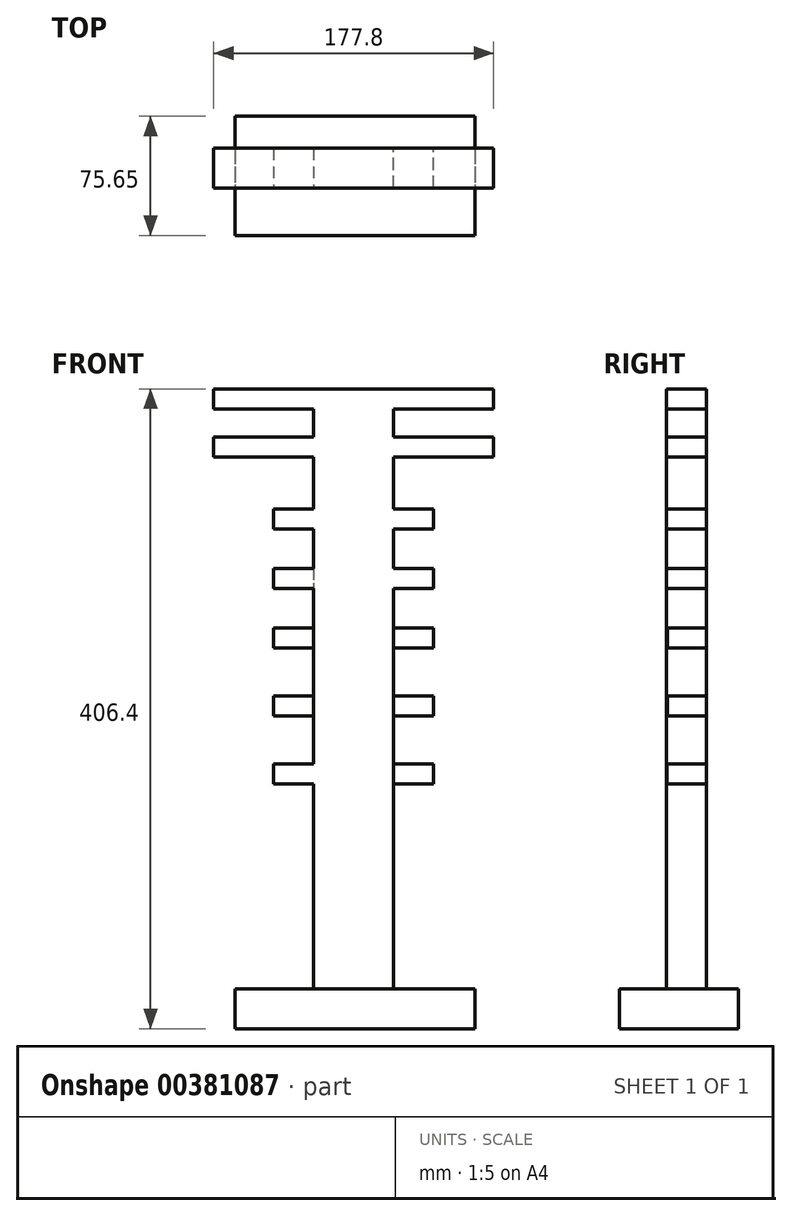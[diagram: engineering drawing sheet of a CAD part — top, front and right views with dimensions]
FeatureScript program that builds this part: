
annotation { "Feature Type Name" : "Feature", "Feature Type Description" : "" }
export const myFeature = defineFeature(function(context is Context, id is Id, definition is map)
    precondition{}
    {
        {
            var Q0;
            Q0=qCreatedBy(makeId("Top.planeOp"),FACE);
            var sketch = newSketch(context, id + "F0", { "sketchPlane" : qUnion([Q0])});
            skLineSegment(sketch, "E0.bottom", {"start": v(-76.2, 0) * mm, "end": v(76.2, 0) * mm});
            skLineSegment(sketch, "E0.top", {"start": v(-76.2, -75.65) * mm, "end": v(76.2, -75.65) * mm});
            skLineSegment(sketch, "E0.left", {"start": v(-76.2, 0) * mm, "end": v(-76.2, -75.65) * mm});
            skLineSegment(sketch, "E0.right", {"start": v(76.2, 0) * mm, "end": v(76.2, -75.65) * mm});
            skSolve(sketch);
        }
        {
            var Q0;
            Q0=makeQuery(id+"F0.imprint","IMPRINT",FACE,{"disambiguationData":[TD([[makeQuery(id+"F0.imprint","IMPRINT",EDGE,{"derivedFrom":sQuery(id+"F0.wireOp",EDGE,"E0.bottom")}),-1.0]])]});
            extrude(context, id + "F1", {"entities" : qUnion([Q0]), "depth" : 25.4 * mm});
        }
        {
            var Q0;
            Q0=makeQuery(id+"F1.opExtrude","CAP_FACE",FACE,{"disambiguationData":[OSD([sQuery(id+"F0.wireOp",EDGE,"E0.bottom"),sQuery(id+"F0.wireOp",EDGE,"E0.top"),sQuery(id+"F0.wireOp",EDGE,"E0.left"),sQuery(id+"F0.wireOp",EDGE,"E0.right")])],"isStart":false});
            var sketch = newSketch(context, id + "F2", { "sketchPlane" : qUnion([Q0])});
            skLineSegment(sketch, "E1.bottom", {"start": v(-26.33, -20.36) * mm, "end": v(24.47, -20.36) * mm});
            skLineSegment(sketch, "E1.top", {"start": v(-26.33, -45.76) * mm, "end": v(24.47, -45.76) * mm});
            skLineSegment(sketch, "E1.left", {"start": v(-26.33, -20.36) * mm, "end": v(-26.33, -45.76) * mm});
            skLineSegment(sketch, "E1.right", {"start": v(24.47, -20.36) * mm, "end": v(24.47, -45.76) * mm});
            skSolve(sketch);
        }
        {
            var Q0;
            Q0=makeQuery(id+"F2.imprint","IMPRINT",FACE,{"disambiguationData":[TD([[makeQuery(id+"F2.imprint","IMPRINT",EDGE,{"derivedFrom":sQuery(id+"F2.wireOp",EDGE,"E1.bottom")}),-1.0]])]});
            extrude(context, id + "F3", {"entities" : qUnion([Q0]), "operationType" : NewBodyOperationType.ADD, "depth" : 381 * mm});
        }
        {
            var Q0;
            Q0=makeQuery(id+"F3.opExtrude","SWEPT_FACE",FACE,{"disambiguationData":[OSD([sQuery(id+"F2.wireOp",EDGE,"E1.right")])]});
            var sketch = newSketch(context, id + "F4", { "sketchPlane" : qUnion([Q0])});
            skLineSegment(sketch, "E2.bottom", {"start": v(-45.76, 406.4) * mm, "end": v(-20.36, 406.4) * mm});
            skLineSegment(sketch, "E2.top", {"start": v(-45.76, 393.7) * mm, "end": v(-20.36, 393.7) * mm});
            skLineSegment(sketch, "E2.left", {"start": v(-45.76, 406.4) * mm, "end": v(-45.76, 393.7) * mm});
            skLineSegment(sketch, "E2.right", {"start": v(-20.36, 406.4) * mm, "end": v(-20.36, 393.7) * mm});
            skSolve(sketch);
        }
        {
            var Q0;
            Q0=makeQuery(id+"F4.imprint","IMPRINT",FACE,{"disambiguationData":[TD([[makeQuery(id+"F4.imprint","IMPRINT",EDGE,{"derivedFrom":sQuery(id+"F4.wireOp",EDGE,"E2.bottom")}),1.0]])]});
            extrude(context, id + "F5", {"entities" : qUnion([Q0]), "operationType" : NewBodyOperationType.ADD, "depth" : 63.5 * mm});
        }
        {
            var Q0;
            Q0=makeQuery(id+"F3.opExtrude","SWEPT_FACE",FACE,{"disambiguationData":[OSD([sQuery(id+"F2.wireOp",EDGE,"E1.right")])]});
            var sketch = newSketch(context, id + "F6", { "sketchPlane" : qUnion([Q0])});
            skLineSegment(sketch, "E3.bottom", {"start": v(-45.76, 375.92) * mm, "end": v(-20.36, 375.92) * mm});
            skLineSegment(sketch, "E3.top", {"start": v(-45.76, 363.22) * mm, "end": v(-20.36, 363.22) * mm});
            skLineSegment(sketch, "E3.left", {"start": v(-45.76, 375.92) * mm, "end": v(-45.76, 363.22) * mm});
            skLineSegment(sketch, "E3.right", {"start": v(-20.36, 375.92) * mm, "end": v(-20.36, 363.22) * mm});
            skSolve(sketch);
        }
        {
            var Q0;
            Q0=makeQuery(id+"F6.imprint","IMPRINT",FACE,{"disambiguationData":[TD([[makeQuery(id+"F6.imprint","IMPRINT",EDGE,{"derivedFrom":sQuery(id+"F6.wireOp",EDGE,"E3.bottom")}),-1.0]])]});
            extrude(context, id + "F7", {"entities" : qUnion([Q0]), "operationType" : NewBodyOperationType.ADD, "depth" : 63.5 * mm});
        }
        {
            var Q0;
            Q0=makeQuery(id+"F3.opExtrude","SWEPT_FACE",FACE,{"disambiguationData":[OSD([sQuery(id+"F2.wireOp",EDGE,"E1.left")])]});
            var sketch = newSketch(context, id + "F8", { "sketchPlane" : qUnion([Q0])});
            skLineSegment(sketch, "E4.bottom", {"start": v(20.36, 406.4) * mm, "end": v(45.76, 406.4) * mm});
            skLineSegment(sketch, "E4.top", {"start": v(20.36, 393.7) * mm, "end": v(45.76, 393.7) * mm});
            skLineSegment(sketch, "E4.left", {"start": v(20.36, 406.4) * mm, "end": v(20.36, 393.7) * mm});
            skLineSegment(sketch, "E4.right", {"start": v(45.76, 406.4) * mm, "end": v(45.76, 393.7) * mm});
            skSolve(sketch);
        }
        {
            var Q0;
            Q0=makeQuery(id+"F8.imprint","IMPRINT",FACE,{"disambiguationData":[TD([[makeQuery(id+"F8.imprint","IMPRINT",EDGE,{"derivedFrom":sQuery(id+"F8.wireOp",EDGE,"E4.bottom")}),-1.0]])]});
            extrude(context, id + "F9", {"entities" : qUnion([Q0]), "operationType" : NewBodyOperationType.ADD, "depth" : 63.5 * mm});
        }
        {
            var Q0;
            Q0=makeQuery(id+"F3.opExtrude","SWEPT_FACE",FACE,{"disambiguationData":[OSD([sQuery(id+"F2.wireOp",EDGE,"E1.left")])]});
            var sketch = newSketch(context, id + "F10", { "sketchPlane" : qUnion([Q0])});
            skLineSegment(sketch, "E5.bottom", {"start": v(20.36, 375.92) * mm, "end": v(45.76, 375.92) * mm});
            skLineSegment(sketch, "E5.top", {"start": v(20.36, 363.22) * mm, "end": v(45.76, 363.22) * mm});
            skLineSegment(sketch, "E5.left", {"start": v(20.36, 375.92) * mm, "end": v(20.36, 363.22) * mm});
            skLineSegment(sketch, "E5.right", {"start": v(45.76, 375.92) * mm, "end": v(45.76, 363.22) * mm});
            skSolve(sketch);
        }
        {
            var Q0;
            Q0=makeQuery(id+"F10.imprint","IMPRINT",FACE,{"disambiguationData":[TD([[makeQuery(id+"F10.imprint","IMPRINT",EDGE,{"derivedFrom":sQuery(id+"F10.wireOp",EDGE,"E5.bottom")}),-1.0]])]});
            extrude(context, id + "F11", {"entities" : qUnion([Q0]), "operationType" : NewBodyOperationType.ADD, "depth" : 63.5 * mm});
        }
        {
            var Q0;
            Q0=makeQuery(id+"F7.boolean.opBoolean","SPLIT",FACE,{"disambiguationData":[TD([makeQuery(id+"F7.opExtrude","SWEPT_FACE",FACE,{"disambiguationData":[OSD([sQuery(id+"F6.wireOp",EDGE,"E3.top")])]})])],"derivedFrom":makeQuery(id+"F3.opExtrude","SWEPT_FACE",FACE,{"disambiguationData":[OSD([sQuery(id+"F2.wireOp",EDGE,"E1.right")])]})});
            var sketch = newSketch(context, id + "F12", { "sketchPlane" : qUnion([Q0])});
            skLineSegment(sketch, "E6.bottom", {"start": v(-45.76, 330.2) * mm, "end": v(-20.36, 330.2) * mm});
            skLineSegment(sketch, "E6.top", {"start": v(-45.76, 317.5) * mm, "end": v(-20.36, 317.5) * mm});
            skLineSegment(sketch, "E6.left", {"start": v(-45.76, 330.2) * mm, "end": v(-45.76, 317.5) * mm});
            skLineSegment(sketch, "E6.right", {"start": v(-20.36, 330.2) * mm, "end": v(-20.36, 317.5) * mm});
            skSolve(sketch);
        }
        {
            var Q0;
            Q0=makeQuery(id+"F12.imprint","IMPRINT",FACE,{"disambiguationData":[TD([[makeQuery(id+"F12.imprint","IMPRINT",EDGE,{"derivedFrom":sQuery(id+"F12.wireOp",EDGE,"E6.bottom")}),-1.0]])]});
            extrude(context, id + "F13", {"entities" : qUnion([Q0]), "operationType" : NewBodyOperationType.ADD, "depth" : 25.4 * mm});
        }
        {
            var Q0;
            Q0=makeQuery(id+"F13.boolean.opBoolean","SPLIT",FACE,{"disambiguationData":[TD([makeQuery(id+"F13.opExtrude","SWEPT_FACE",FACE,{"disambiguationData":[OSD([sQuery(id+"F12.wireOp",EDGE,"E6.top")])]})])],"derivedFrom":makeQuery(id+"F7.boolean.opBoolean","SPLIT",FACE,{"disambiguationData":[TD([makeQuery(id+"F7.opExtrude","SWEPT_FACE",FACE,{"disambiguationData":[OSD([sQuery(id+"F6.wireOp",EDGE,"E3.top")])]})])],"derivedFrom":makeQuery(id+"F3.opExtrude","SWEPT_FACE",FACE,{"disambiguationData":[OSD([sQuery(id+"F2.wireOp",EDGE,"E1.right")])]})})});
            var sketch = newSketch(context, id + "F14", { "sketchPlane" : qUnion([Q0])});
            skLineSegment(sketch, "E7.bottom", {"start": v(-45.76, 292.35) * mm, "end": v(-20.36, 292.35) * mm});
            skLineSegment(sketch, "E7.top", {"start": v(-45.76, 279.65) * mm, "end": v(-20.36, 279.65) * mm});
            skLineSegment(sketch, "E7.left", {"start": v(-45.76, 292.35) * mm, "end": v(-45.76, 279.65) * mm});
            skLineSegment(sketch, "E7.right", {"start": v(-20.36, 292.35) * mm, "end": v(-20.36, 279.65) * mm});
            skSolve(sketch);
        }
        {
            var Q0;
            {var subQ0=sQuery(id+"F14.wireOp",EDGE,"E7.top");Q0=makeQuery(id+"F14.imprint","IMPRINT",FACE,{"disambiguationData":[TD([[makeQuery(id+"F14.imprint","IMPRINT",EDGE,{"derivedFrom":subQ0}),-1.0]])]});}
            var sketch = newSketch(context, id + "F15", { "sketchPlane" : qUnion([Q0])});
            skLineSegment(sketch, "E8.bottom", {"start": v(-45.28, 254.5) * mm, "end": v(-19.88, 254.5) * mm});
            skLineSegment(sketch, "E8.top", {"start": v(-45.28, 241.8) * mm, "end": v(-19.88, 241.8) * mm});
            skLineSegment(sketch, "E8.left", {"start": v(-45.28, 254.5) * mm, "end": v(-45.28, 241.8) * mm});
            skLineSegment(sketch, "E8.right", {"start": v(-19.88, 254.5) * mm, "end": v(-19.88, 241.8) * mm});
            skSolve(sketch);
        }
        {
            var Q0;
            {var subQ2=sQuery(id+"F15.wireOp",EDGE,"E8.left");Q0=makeQuery(id+"F15.imprint","IMPRINT",FACE,{"disambiguationData":[TD([[makeQuery(id+"F15.imprint","IMPRINT",EDGE,{"derivedFrom":subQ2}),-1.0]])]});}
            var sketch = newSketch(context, id + "F16", { "sketchPlane" : qUnion([Q0])});
            skLineSegment(sketch, "E9.bottom", {"start": v(-45.32, 211.33) * mm, "end": v(-19.92, 211.33) * mm});
            skLineSegment(sketch, "E9.top", {"start": v(-45.32, 198.63) * mm, "end": v(-19.92, 198.63) * mm});
            skLineSegment(sketch, "E9.left", {"start": v(-45.32, 211.33) * mm, "end": v(-45.32, 198.63) * mm});
            skLineSegment(sketch, "E9.right", {"start": v(-19.92, 211.33) * mm, "end": v(-19.92, 198.63) * mm});
            skSolve(sketch);
        }
        {
            var Q0;
            {var subQ27=sQuery(id+"F16.wireOp",EDGE,"E9.left");Q0=makeQuery(id+"F16.imprint","IMPRINT",FACE,{"disambiguationData":[TD([[makeQuery(id+"F16.imprint","IMPRINT",EDGE,{"derivedFrom":subQ27}),-1.0]])]});}
            var sketch = newSketch(context, id + "F17", { "sketchPlane" : qUnion([Q0])});
            skLineSegment(sketch, "E10.bottom", {"start": v(-45.37, 168.15) * mm, "end": v(-19.97, 168.15) * mm});
            skLineSegment(sketch, "E10.top", {"start": v(-45.37, 155.45) * mm, "end": v(-19.97, 155.45) * mm});
            skLineSegment(sketch, "E10.left", {"start": v(-45.37, 168.15) * mm, "end": v(-45.37, 155.45) * mm});
            skLineSegment(sketch, "E10.right", {"start": v(-19.97, 168.15) * mm, "end": v(-19.97, 155.45) * mm});
            skSolve(sketch);
        }
        {
            var Q0;
            Q0=makeQuery(id+"F14.imprint","IMPRINT",FACE,{"disambiguationData":[TD([[makeQuery(id+"F14.imprint","IMPRINT",EDGE,{"derivedFrom":sQuery(id+"F14.wireOp",EDGE,"E7.bottom")}),-1.0]])]});
            extrude(context, id + "F18", {"entities" : qUnion([Q0]), "operationType" : NewBodyOperationType.ADD, "depth" : 25.4 * mm});
        }
        {
            var Q0;
            {var subQ0=sQuery(id+"F15.wireOp",EDGE,"E8.left");Q0=makeQuery(id+"F15.imprint","IMPRINT",FACE,{"disambiguationData":[TD([[makeQuery(id+"F15.imprint","IMPRINT",EDGE,{"derivedFrom":subQ0}),1.0]])]});}
            extrude(context, id + "F19", {"entities" : qUnion([Q0]), "operationType" : NewBodyOperationType.ADD, "depth" : 25.4 * mm});
        }
        {
            var Q0;
            {var subQ0=sQuery(id+"F16.wireOp",EDGE,"E9.left");Q0=makeQuery(id+"F16.imprint","IMPRINT",FACE,{"disambiguationData":[TD([[makeQuery(id+"F16.imprint","IMPRINT",EDGE,{"derivedFrom":subQ0}),1.0]])]});}
            extrude(context, id + "F20", {"entities" : qUnion([Q0]), "operationType" : NewBodyOperationType.ADD, "depth" : 25.4 * mm});
        }
        {
            var Q0;
            {var subQ0=sQuery(id+"F17.wireOp",EDGE,"E10.left");Q0=makeQuery(id+"F17.imprint","IMPRINT",FACE,{"disambiguationData":[TD([[makeQuery(id+"F17.imprint","IMPRINT",EDGE,{"derivedFrom":subQ0}),1.0]])]});}
            extrude(context, id + "F21", {"entities" : qUnion([Q0]), "operationType" : NewBodyOperationType.ADD, "depth" : 25.4 * mm});
        }
        {
            var Q0;
            Q0=makeQuery(id+"F11.boolean.opBoolean","SPLIT",FACE,{"disambiguationData":[TD([makeQuery(id+"F11.opExtrude","SWEPT_FACE",FACE,{"disambiguationData":[OSD([sQuery(id+"F10.wireOp",EDGE,"E5.top")])]})])],"derivedFrom":makeQuery(id+"F3.opExtrude","SWEPT_FACE",FACE,{"disambiguationData":[OSD([sQuery(id+"F2.wireOp",EDGE,"E1.left")])]})});
            var sketch = newSketch(context, id + "F22", { "sketchPlane" : qUnion([Q0])});
            skLineSegment(sketch, "E11.bottom", {"start": v(20.36, 330.2) * mm, "end": v(45.76, 330.2) * mm});
            skLineSegment(sketch, "E11.top", {"start": v(20.36, 317.5) * mm, "end": v(45.76, 317.5) * mm});
            skLineSegment(sketch, "E11.left", {"start": v(20.36, 330.2) * mm, "end": v(20.36, 317.5) * mm});
            skLineSegment(sketch, "E11.right", {"start": v(45.76, 330.2) * mm, "end": v(45.76, 317.5) * mm});
            skSolve(sketch);
        }
        {
            var Q0;
            {var subQ0=sQuery(id+"F22.wireOp",EDGE,"E11.top");Q0=makeQuery(id+"F22.imprint","IMPRINT",FACE,{"disambiguationData":[TD([[makeQuery(id+"F22.imprint","IMPRINT",EDGE,{"derivedFrom":subQ0}),-1.0]])]});}
            var sketch = newSketch(context, id + "F23", { "sketchPlane" : qUnion([Q0])});
            skLineSegment(sketch, "E12.bottom", {"start": v(20.44, 292.35) * mm, "end": v(45.84, 292.35) * mm});
            skLineSegment(sketch, "E12.top", {"start": v(20.44, 279.65) * mm, "end": v(45.84, 279.65) * mm});
            skLineSegment(sketch, "E12.left", {"start": v(20.44, 292.35) * mm, "end": v(20.44, 279.65) * mm});
            skLineSegment(sketch, "E12.right", {"start": v(45.84, 292.35) * mm, "end": v(45.84, 279.65) * mm});
            skSolve(sketch);
        }
        {
            var Q0;
            {var subQ2=sQuery(id+"F23.wireOp",EDGE,"E12.left");Q0=makeQuery(id+"F23.imprint","IMPRINT",FACE,{"disambiguationData":[TD([[makeQuery(id+"F23.imprint","IMPRINT",EDGE,{"derivedFrom":subQ2}),-1.0]])]});}
            var sketch = newSketch(context, id + "F24", { "sketchPlane" : qUnion([Q0])});
            skLineSegment(sketch, "E13.bottom", {"start": v(20.29, 254.5) * mm, "end": v(45.69, 254.5) * mm});
            skLineSegment(sketch, "E13.top", {"start": v(20.29, 241.8) * mm, "end": v(45.69, 241.8) * mm});
            skLineSegment(sketch, "E13.left", {"start": v(20.29, 254.5) * mm, "end": v(20.29, 241.8) * mm});
            skLineSegment(sketch, "E13.right", {"start": v(45.69, 254.5) * mm, "end": v(45.69, 241.8) * mm});
            skSolve(sketch);
        }
        {
            var Q0;
            {var subQ0=sQuery(id+"F22.wireOp",EDGE,"E11.top");Q0=makeQuery(id+"F22.imprint","IMPRINT",FACE,{"disambiguationData":[TD([[makeQuery(id+"F22.imprint","IMPRINT",EDGE,{"derivedFrom":subQ0}),-1.0]])]});}
            var sketch = newSketch(context, id + "F25", { "sketchPlane" : qUnion([Q0])});
            skLineSegment(sketch, "E14.bottom", {"start": v(20.09, 211.33) * mm, "end": v(45.49, 211.33) * mm});
            skLineSegment(sketch, "E14.top", {"start": v(20.09, 198.63) * mm, "end": v(45.49, 198.63) * mm});
            skLineSegment(sketch, "E14.left", {"start": v(20.09, 211.33) * mm, "end": v(20.09, 198.63) * mm});
            skLineSegment(sketch, "E14.right", {"start": v(45.49, 211.33) * mm, "end": v(45.49, 198.63) * mm});
            skSolve(sketch);
        }
        {
            var Q0;
            {var subQ0=sQuery(id+"F25.wireOp",EDGE,"E14.right");Q0=makeQuery(id+"F25.imprint","IMPRINT",FACE,{"disambiguationData":[TD([[makeQuery(id+"F25.imprint","IMPRINT",EDGE,{"derivedFrom":subQ0}),1.0]])]});}
            var sketch = newSketch(context, id + "F26", { "sketchPlane" : qUnion([Q0])});
            skLineSegment(sketch, "E15.bottom", {"start": v(19.82, 168.15) * mm, "end": v(46.54, 168.15) * mm});
            skLineSegment(sketch, "E15.top", {"start": v(19.82, 155.45) * mm, "end": v(46.54, 155.45) * mm});
            skLineSegment(sketch, "E15.left", {"start": v(19.82, 168.15) * mm, "end": v(19.82, 155.45) * mm});
            skLineSegment(sketch, "E15.right", {"start": v(46.54, 168.15) * mm, "end": v(46.54, 155.45) * mm});
            skSolve(sketch);
        }
        {
            var Q0;
            Q0=makeQuery(id+"F22.imprint","IMPRINT",FACE,{"disambiguationData":[TD([[makeQuery(id+"F22.imprint","IMPRINT",EDGE,{"derivedFrom":sQuery(id+"F22.wireOp",EDGE,"E11.bottom")}),-1.0]])]});
            extrude(context, id + "F27", {"entities" : qUnion([Q0]), "operationType" : NewBodyOperationType.ADD, "depth" : 25.4 * mm});
        }
        {
            var Q0;
            {var subQ0=sQuery(id+"F23.wireOp",EDGE,"E12.left");Q0=makeQuery(id+"F23.imprint","IMPRINT",FACE,{"disambiguationData":[TD([[makeQuery(id+"F23.imprint","IMPRINT",EDGE,{"derivedFrom":subQ0}),1.0]])]});}
            extrude(context, id + "F28", {"entities" : qUnion([Q0]), "operationType" : NewBodyOperationType.ADD, "depth" : 25.4 * mm});
        }
        {
            var Q0;
            {var subQ0=sQuery(id+"F24.wireOp",EDGE,"E13.right");Q0=makeQuery(id+"F24.imprint","IMPRINT",FACE,{"disambiguationData":[TD([[makeQuery(id+"F24.imprint","IMPRINT",EDGE,{"derivedFrom":subQ0}),-1.0]])]});}
            extrude(context, id + "F29", {"entities" : qUnion([Q0]), "operationType" : NewBodyOperationType.ADD, "depth" : 25.4 * mm});
        }
        {
            var Q0;
            {var subQ0=sQuery(id+"F25.wireOp",EDGE,"E14.right");Q0=makeQuery(id+"F25.imprint","IMPRINT",FACE,{"disambiguationData":[TD([[makeQuery(id+"F25.imprint","IMPRINT",EDGE,{"derivedFrom":subQ0}),-1.0]])]});}
            extrude(context, id + "F30", {"entities" : qUnion([Q0]), "operationType" : NewBodyOperationType.ADD, "depth" : 25.4 * mm});
        }
        {
            var Q0;
            {var subQ0=sQuery(id+"F26.wireOp",EDGE,"E15.bottom");var subQ2=sQuery(id+"F2.wireOp",EDGE,"E1.left");var subQ5=makeQuery(id+"F11.opExtrude","SWEPT_FACE",FACE,{"disambiguationData":[OSD([sQuery(id+"F10.wireOp",EDGE,"E5.top")])]});var subQ7=makeQuery(id+"F3.opExtrude","CAP_EDGE",EDGE,{"disambiguationData":[OSD([subQ2])],"isStart":true});var subQ12=sQuery(id+"F2.wireOp",EDGE,"E1.top");var subQ13=makeQuery(id+"F11.boolean.opBoolean","SPLIT",EDGE,{"disambiguationData":[TD([subQ5])],"derivedFrom":makeQuery(id+"F3.opExtrude","SWEPT_EDGE",EDGE,{"disambiguationData":[OSD([subQ12,subQ2])]})});var subQ14=makeQuery(id+"F25.imprint","IMPRINT",EDGE,{"derivedFrom":makeQuery(id+"F22.imprint","IMPRINT",EDGE,{"disambiguationData":[TD([[makeQuery(id+"F22.imprint","INTERSECT",VERTEX,{"derivedFrom":[subQ7,subQ13]}),1.0]])],"derivedFrom":subQ13})});var subQ15=makeQuery(id+"F26.imprint","INTERSECT",VERTEX,{"derivedFrom":[subQ14,subQ0]});Q0=makeQuery(id+"F26.imprint","IMPRINT",FACE,{"disambiguationData":[TD([[makeQuery(id+"F26.imprint","IMPRINT",EDGE,{"disambiguationData":[TD([[subQ15,-1.0]])],"derivedFrom":subQ14}),-1.0]])]});}
            extrude(context, id + "F31", {"entities" : qUnion([Q0]), "operationType" : NewBodyOperationType.ADD, "depth" : 25.4 * mm});
        }
    });
